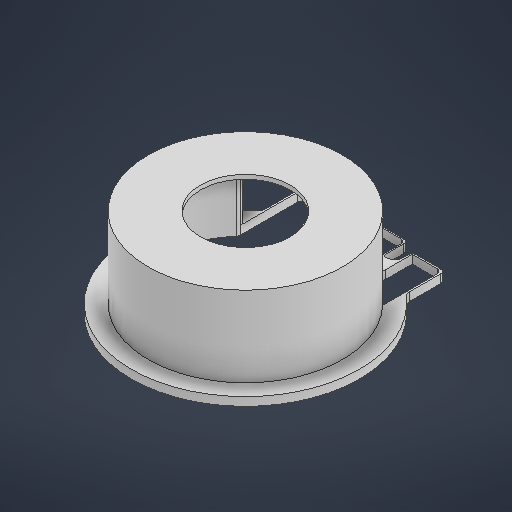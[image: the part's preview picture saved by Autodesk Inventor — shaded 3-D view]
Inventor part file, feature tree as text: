
AUTODESK INVENTOR PART (.ipt)
format: ipt  version: 2025 (Build 290162000, 162)  size: 378,368 bytes
history: native  units: in
note: dims shown in document units (in); Inventor stores cm internally (conversion verified against a paired STEP export)
features: other x12, extrude x6, fillet x5, sketch x3
ambient origin geometry x8: Origin, YZ Plane, XZ Plane, XY Plane, X Axis, Y Axis, Z Axis, Center Point
bodies: Solid1 (feature_tree)
feature tree (26):
  other  "Table"
  other  "Cylinder Segment - 01"
  other  "Cylinder Segment - 02"
  other  "Cylinder Segment - 03"
  other  "Cylinder Segment - 04"
  other  "Cylinder Segment - 05"
  other  "Cylinder Segment - 06"
  other  "Cylinder Segment - 07"
  other  "Cylinder Segment - 08"
  other  "Cylinder Segment - 09"
  other  "Cylinder Segment - 10"
  other  "Cylinder Segment - Face"
  sketch  "Sketch1"  dims[d5=0.0in d7=0.0in]
  extrude  "Extrusion1"  TaperAngle=0.0deg  [1 undecoded]
  extrude  "Extrusion2"  Depth=4.5276in
  extrude  "Extrusion7"  Depth=2.5591in
  sketch  "Sketch24"  dims[d234=0.0787in d235=2.5591in d237=0.0591in d238=2.564in d240=0.8253in d241=10.6299in d242=2.7608in d243=0.5433in d244=1.5298in d247=0.0787in d248=3.5433in d249=3.6614in d250=0.0in d251=3.6614in d252=0.0in d253=9.4488in d254=0.3937in d255=0.0in d256=0.3937in d257=0.3937in d258=0.0787in d259=0.1969in d260=0.1969in d113=0.0197in d114=0.0344in d115=0.0197in d116=0.0344in d167=0.0197in d168=0.0344in d169=0.0197in d170=0.0344in d215=0.0197in d216=0.0344in d217=0.0197in d218=0.0344in d219=0.0in d220=0.0in]
  extrude  "Extrusion30"  Depth=0.0591in
  extrude  "Extrusion31"  Depth=0.1969in
  extrude  "Extrusion32"  Depth=0.1969in
  fillet  "Fillet14"  Radius=10.6299in
  fillet  "Fillet15"  Radius=2.7608in
  fillet  "Fillet16"  Radius=0.5433in
  fillet  "Fillet17"  Radius=1.5298in
  fillet  "Fillet18"  Radius=0.0787in
  sketch  "Sketch2"  dims[d18=0.0in d52=4.5276in]
note: 1 required parameter value undecoded (feature->parameter linkage not recoverable at this tier; creation-order binding heuristic only, values carry confidence <= 0.55)
